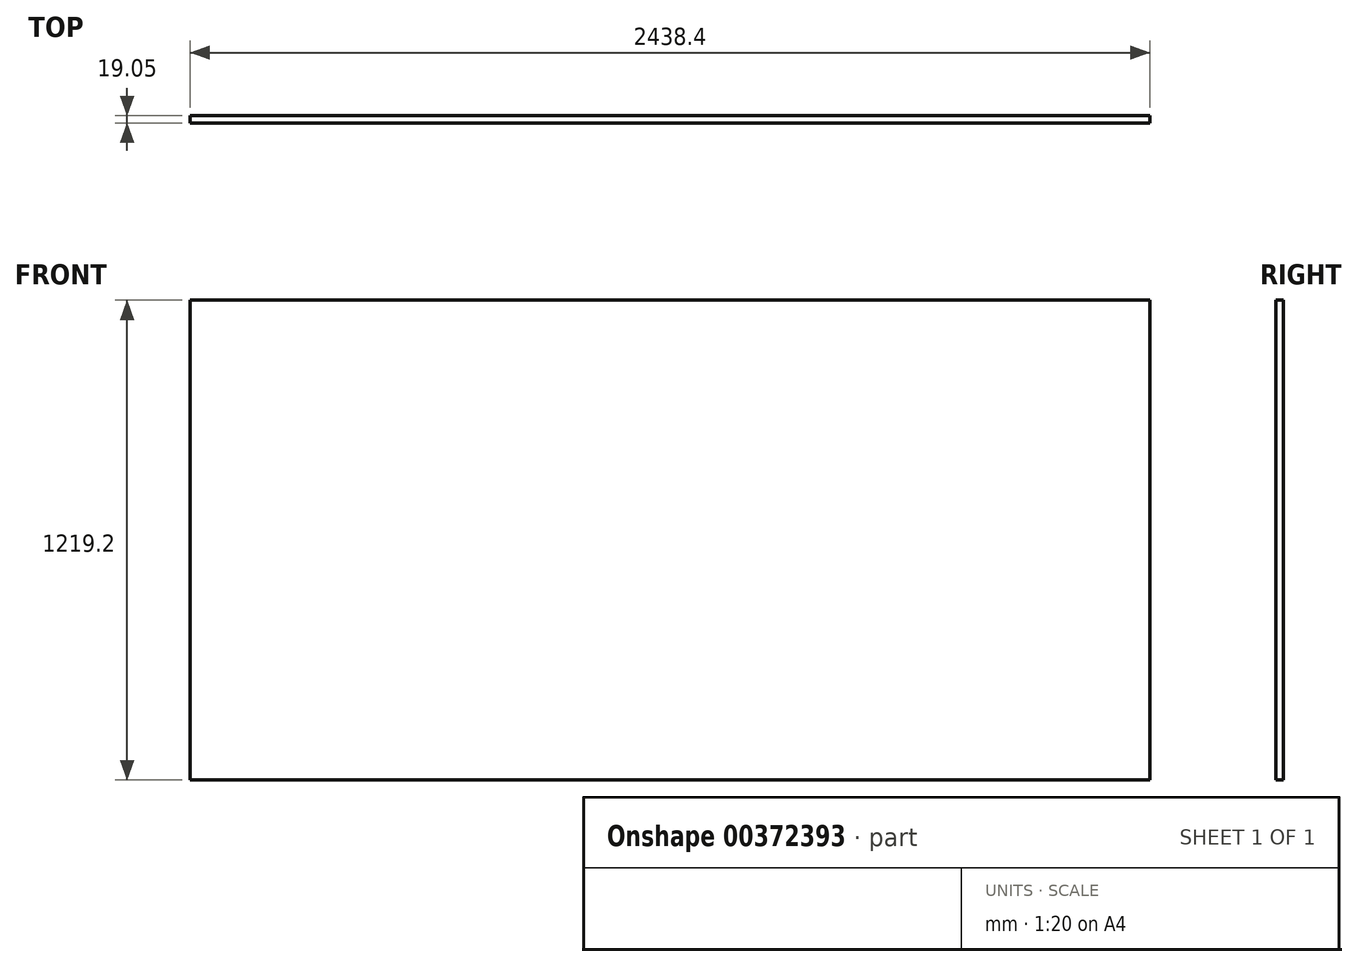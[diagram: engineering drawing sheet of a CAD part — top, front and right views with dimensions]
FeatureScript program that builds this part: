
annotation { "Feature Type Name" : "Feature", "Feature Type Description" : "" }
export const myFeature = defineFeature(function(context is Context, id is Id, definition is map)
    precondition{}
    {
        {
            var Q0;
            Q0=qCreatedBy(makeId("Front.planeOp"),FACE);
            var sketch = newSketch(context, id + "F0", { "sketchPlane" : qUnion([Q0])});
            skLineSegment(sketch, "E0.bottom", {"start": v(1219.2, -609.6) * mm, "end": v(-1219.2, -609.6) * mm});
            skLineSegment(sketch, "E0.top", {"start": v(1219.2, 609.6) * mm, "end": v(-1219.2, 609.6) * mm});
            skLineSegment(sketch, "E0.left", {"start": v(1219.2, -609.6) * mm, "end": v(1219.2, 609.6) * mm});
            skLineSegment(sketch, "E0.right", {"start": v(-1219.2, -609.6) * mm, "end": v(-1219.2, 609.6) * mm});
            skPoint(sketch, "E0.middle", {"position": v(0, 0) * mm});
            skSolve(sketch);
        }
        {
            var Q0;
            Q0=qSketchRegion(id+"F0",true);
            extrude(context, id + "F1", {"entities" : qUnion([Q0]), "depth" : 19.05 * mm});
        }
    });
